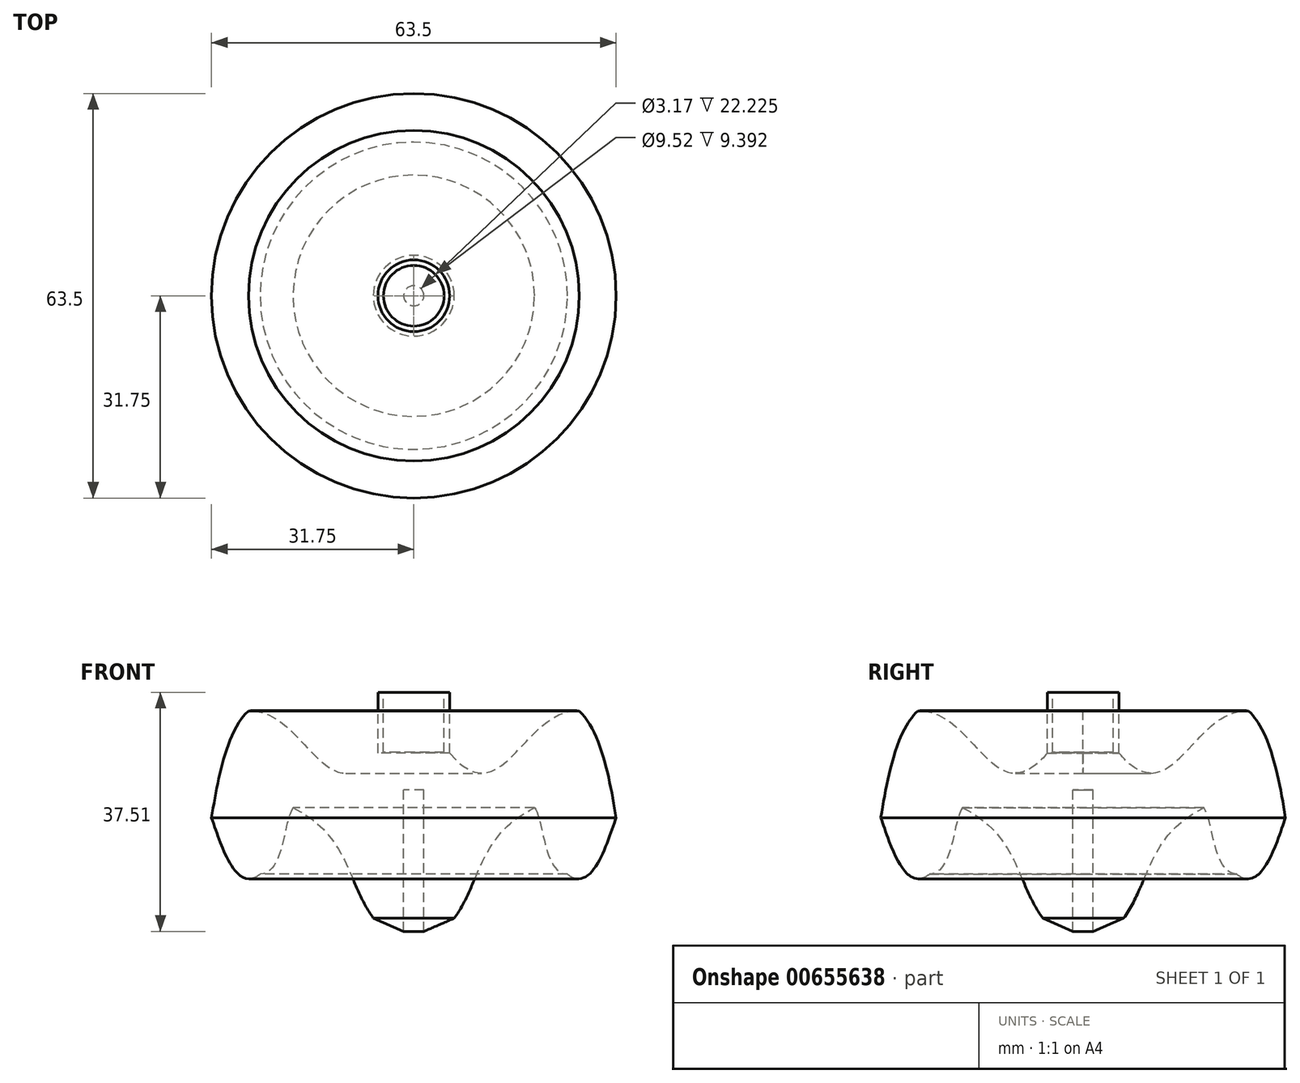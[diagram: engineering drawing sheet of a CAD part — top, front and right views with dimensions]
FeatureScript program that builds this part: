
annotation { "Feature Type Name" : "Feature", "Feature Type Description" : "" }
export const myFeature = defineFeature(function(context is Context, id is Id, definition is map)
    precondition{}
    {
        {
            var Q0;
            Q0=qCreatedBy(makeId("Front.planeOp"),FACE);
            var sketch = newSketch(context, id + "F0", { "sketchPlane" : qUnion([Q0])});
            skLineSegment(sketch, "E0", {"start": v(0, 0) * mm, "end": v(0, 22.23) * mm});
            skLineSegment(sketch, "E1", {"start": v(0, 22.23) * mm, "end": v(1.59, 22.23) * mm});
            skLineSegment(sketch, "E2", {"start": v(1.59, 22.23) * mm, "end": v(1.59, 0) * mm});
            skLineSegment(sketch, "E3", {"start": v(1.59, 0) * mm, "end": v(6.34, 2.05) * mm});
            skLineSegment(sketch, "E4", {"start": v(5.63, 27.98) * mm, "end": v(5.63, 37.5) * mm});
            skLineSegment(sketch, "E5", {"start": v(5.63, 37.5) * mm, "end": v(4.76, 37.5) * mm});
            skLineSegment(sketch, "E6", {"start": v(0, 28.1) * mm, "end": v(0, 0) * mm});
            skLineSegment(sketch, "E7", {"start": v(4.76, 37.5) * mm, "end": v(4.76, 28.12) * mm});
            skLineSegment(sketch, "E8", {"start": v(4.76, 28.12) * mm, "end": v(0, 28.1) * mm});
            skFitSpline(sketch, "E9", {"points": [v(6.34, 2.05) * mm, v(18.94, 19.4) * mm], "startDerivative": vector(12.6, 17.35) * mm, "endDerivative": vector(26.31, 13.1) * mm});
            skFitSpline(sketch, "E10", {"points": [v(18.94, 19.4) * mm, v(24.12, 8.97) * mm], "startDerivative": vector(4.85, -7.06) * mm, "endDerivative": vector(11.49, -0.73) * mm});
            skFitSpline(sketch, "E11", {"points": [v(24.12, 8.97) * mm, v(31.75, 17.82) * mm], "startDerivative": vector(12.12, -9.77) * mm, "endDerivative": vector(3.89, 10.44) * mm});
            skFitSpline(sketch, "E12", {"points": [v(31.75, 17.82) * mm, v(25.95, 34.61) * mm], "startDerivative": vector(-2.84, 16.84) * mm, "endDerivative": vector(-10.72, 10.07) * mm});
            skFitSpline(sketch, "E13", {"points": [v(5.63, 27.98) * mm, v(25.95, 34.61) * mm], "startDerivative": vector(25.13, -30.04) * mm, "endDerivative": vector(26.13, -1.4) * mm});
            skSolve(sketch);
        }
        {
            var Q0;
            Q0 = qSketchRegion(id + "F0", true);
            var Q1;
            Q1=sQuery(id+"F0.wireOp",EDGE,"E6");
            revolve(context, id + "F1", {"entities" : qUnion([Q0]), "axis" : qUnion([Q1]), "revolveType" : RevolveType.FULL});
        }
    });
